# Revit family: CONV_Pholc_GnrlPrpseLmnrs_BlendFloor
name_source: partatom
category: Lighting Fixtures
revit_build: Autodesk Revit 2015 (Build: 20140606_1530(x64)
units: mm (PartAtom-declared; Revit-internal decimal feet)

## types (2) — shared parameters
Apparent Load = 0 VA
AssetType = Fixed
BIMObjectName = CONV_Pholc_GnrlPrpseLmnrs_BlendFloor
Brand = Pholc
BulbIncluded = Yes
CableLength = 2000 mm  [stored 6.56168 ft]
Category = Floor lamps
Collection = North & East
Color Filter = 16777215
ConvergoRefNr = 0103-1704-0010-SE
Designer = Sabina Grubbeson
Dimmer = Yes
Dimming Lamp Color Temperature Shift = <None>
DurationUnit = Year
ExpiringDate = 12/2017
Finish = Polished
HasProtectiveEarth = No
IfcExportAs = IfcLightFixtureType
IfcExportType = NOTDEFINED
Light Source Symbol Length = 150 mm
LightFixtureSecondaryMaterial = Brass
ManufacterURL = www.pholc.se
Manufacturer = Pholc
ManufacturerName = Pholc
Material = Steel&Brass
MaxWatt = 20 W
Model = Blend Floor
NBSDescription = General purpose luminaires
NBSReference = 90-60-50/405
Name = GnrlPrpseLmnrs_BlendFloor
NominalCurrent = 0 A
NominalDepth = 280 mm  [stored 0.918635 ft]
NominalFrequencyRange = 0 Hz
NominalHeight = 1500 mm  [stored 4.92126 ft]
NominalVoltage = 0 V
NominalVoltageCalc = 0 V
NominalWidth = 280 mm  [stored 0.918635 ft]
NumberOfPoles = 1
On/OffSwitch = Yes
PhaseAngle = 0.00°
Shape = Sculptured
Size = 280x280x320mm
Socket = G4 Base
Spot Beam Angle = 30.00°
Spot Field Angle = 110.00°
Tilt Angle = 30.00°
TotalWattage = 0 W
URL = http://www.pholc.se
Uniclass2 = Pr_70_70_49
Uniclass2015Description = Luminaires, lighting track and lighting accessories
Uniclass2015Reference = Pr_70_70_48
UsageCurrent = 0 A
Version = 1
VersionDate = 12/05/2017
WarrantyDurationUnit = Year
Weight = 3.6 kg
zero-valued in all types: DefaultElevation, ElectricalDeviceNominalPower, MaintenanceFactor, NumberOfSources

## per-type parameters (varying)
| type | ArticleNumber | Color | LightFixtureMainMaterial | LightFixtureTertitaryMaterial | ModelNumber |
| Black/brass | 101415 | Yellow&Black | Black Steel | Black textile | 101415 |
| White/brass | 101413 | Yellow&White | White Steel | White Textile | 101413 |

note: [stored X ft] marks values corroborated as IEEE doubles in the binary element streams (Revit-internal decimal feet)

## geometry (parser evidence)
native form markers: Blend x12, Sweep x2
no freeform markers — native parametric forms only
